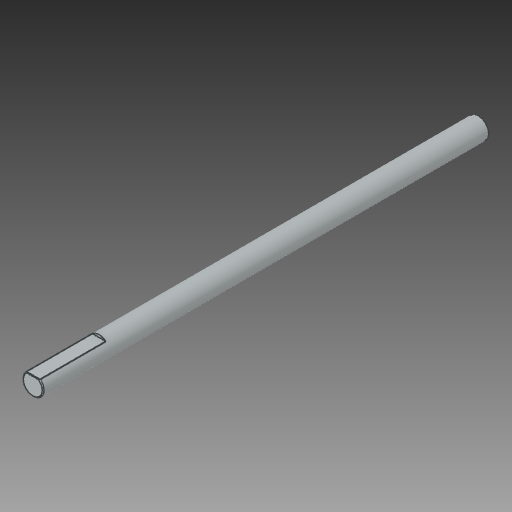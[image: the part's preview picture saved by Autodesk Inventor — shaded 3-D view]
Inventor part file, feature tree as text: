
AUTODESK INVENTOR PART (.ipt)
format: ipt  version: 2018 (Build 220112000, 112)  size: 101,376 bytes
history: native  units: mm
features: other x1, fillet x1
ambient origin geometry x8: Origin, YZ Plane, XZ Plane, XY Plane, X Axis, Y Axis, Z Axis, Center Point
bodies: Body1 (feature_tree)
feature tree (2):
  other  "ソリッド1"
  fillet  "Fillet2"  [1 undecoded]
note: 1 required parameter value undecoded (feature->parameter linkage not recoverable at this tier; creation-order binding heuristic only, values carry confidence <= 0.55)
